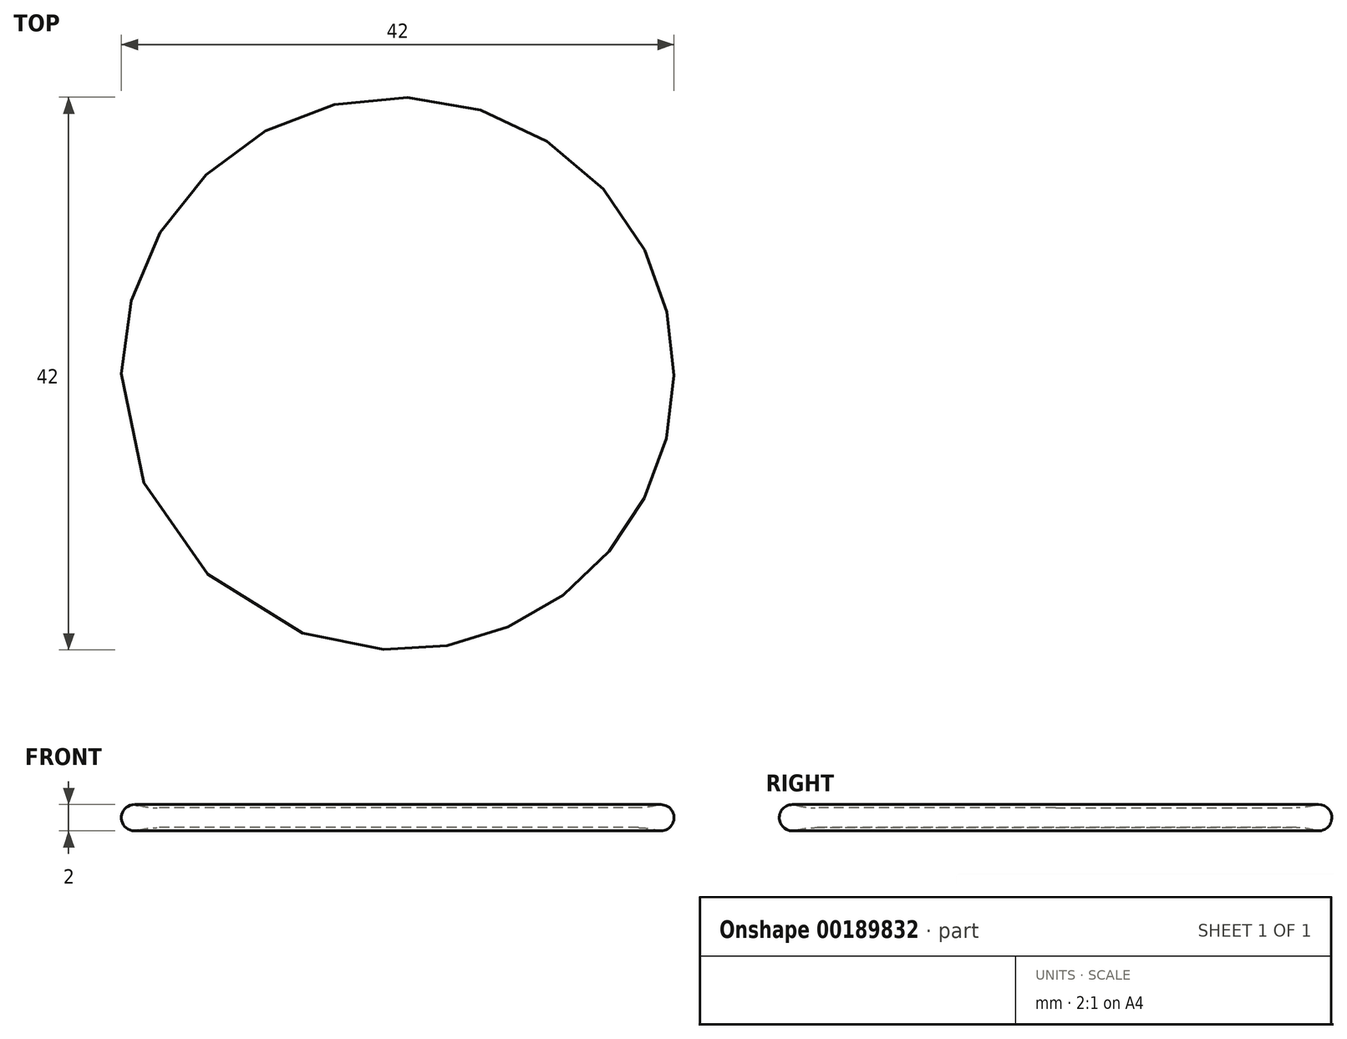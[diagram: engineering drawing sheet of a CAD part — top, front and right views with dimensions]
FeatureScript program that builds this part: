
annotation { "Feature Type Name" : "Feature", "Feature Type Description" : "" }
export const myFeature = defineFeature(function(context is Context, id is Id, definition is map)
    precondition{}
    {
        {
            var Q0;
            Q0=qCreatedBy(makeId("Top.planeOp"),FACE);
            var sketch = newSketch(context, id + "F0", { "sketchPlane" : qUnion([Q0])});
            skCircle(sketch, "E0", {"center": v(0, 0) * mm, "radius": 20 * mm});
            skSolve(sketch);
        }
        {
            var Q0;
            Q0=qCreatedBy(makeId("Front.planeOp"),FACE);
            var sketch = newSketch(context, id + "F1", { "sketchPlane" : qUnion([Q0])});
            skLineSegment(sketch, "E1.0", {"start": v(-20, 0) * mm, "end": v(20, 0) * mm});
            skCircle(sketch, "E2", {"center": v(-20, 0) * mm, "radius": 1 * mm});
            skSolve(sketch);
        }
        {
            var Q0;
            Q0=makeQuery(id+"F1.imprint","IMPRINT",FACE,{"disambiguationData":[TD([[makeQuery(id+"F1.imprint","IMPRINT",EDGE,{"derivedFrom":sQuery(id+"F1.wireOp",EDGE,"E2")}),1.0]])]});
            var Q1;
            Q1=sQuery(id+"F0.wireOp",EDGE,"E0");
            revolve(context, id + "F2", {"entities" : qUnion([Q0]), "axis" : qUnion([Q1]), "revolveType" : RevolveType.FULL});
        }
        {
            var Q0;
            Q0=makeQuery(id+"F0.imprint","IMPRINT",FACE,{"disambiguationData":[TD([[makeQuery(id+"F0.imprint","IMPRINT",EDGE,{"derivedFrom":sQuery(id+"F0.wireOp",EDGE,"E0")}),1.0]])]});
            extrude(context, id + "F3", {"entities" : qUnion([Q0]), "operationType" : NewBodyOperationType.ADD, "depth" : .75 * mm, "hasSecondDirection" : true, "secondDirectionOppositeDirection" : true, "secondDirectionDepth" : .75 * mm});
        }
        {
            var Q0;
            Q0=makeQuery(id+"F3.boolean.opBoolean","INTERSECT",EDGE,{"derivedFrom":[makeQuery(id+"F2.opRevolve","SWEPT_FACE",FACE,{"disambiguationData":[OSD([sQuery(id+"F1.wireOp",EDGE,"E2")])]}),makeQuery(id+"F3.opExtrude","CAP_FACE",FACE,{"disambiguationData":[OSD([sQuery(id+"F0.wireOp",EDGE,"E0")])],"isStart":false})]});
            var Q1;
            Q1=makeQuery(id+"F3.boolean.opBoolean","INTERSECT",EDGE,{"derivedFrom":[makeQuery(id+"F2.opRevolve","SWEPT_FACE",FACE,{"disambiguationData":[OSD([sQuery(id+"F1.wireOp",EDGE,"E2")])]}),makeQuery(id+"F3.opExtrude","CAP_FACE",FACE,{"disambiguationData":[OSD([sQuery(id+"F0.wireOp",EDGE,"E0")])],"isStart":true})]});
            fillet(context, id + "F4", {"entities" : qUnion([Q0, Q1]), "radius" : 5 * mm, "tangentPropagation" : true, "allowEdgeOverflow" : false});
        }
    });
